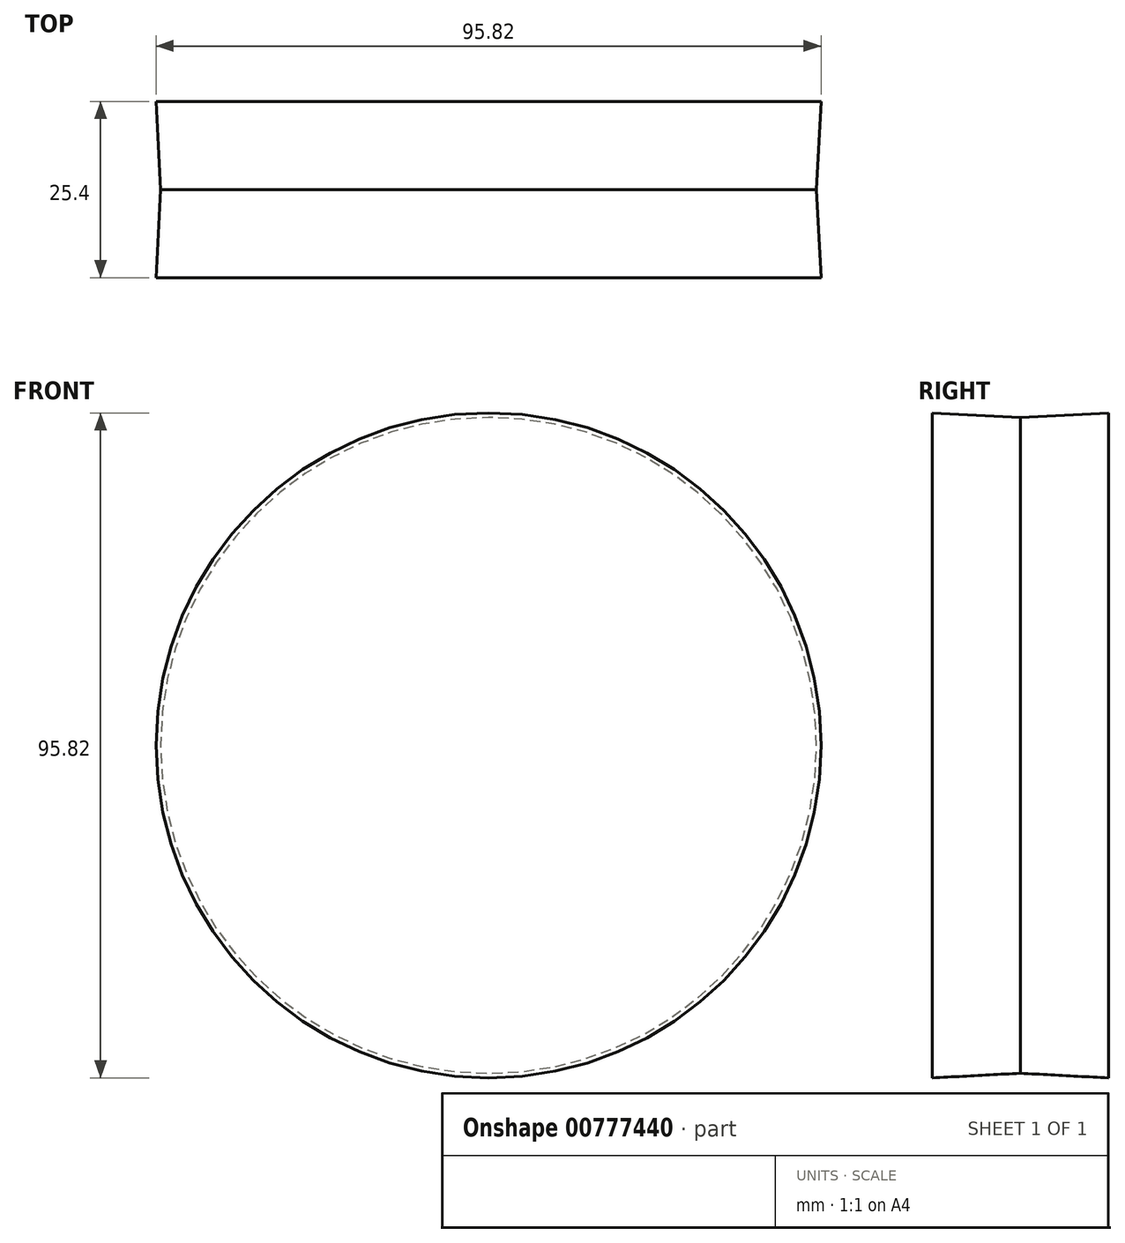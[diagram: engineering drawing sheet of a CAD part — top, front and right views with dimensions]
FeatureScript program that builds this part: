
annotation { "Feature Type Name" : "Feature", "Feature Type Description" : "" }
export const myFeature = defineFeature(function(context is Context, id is Id, definition is map)
    precondition{}
    {
        {
            var Q0;
            Q0=qCreatedBy(makeId("Front.planeOp"),FACE);
            var sketch = newSketch(context, id + "F0", { "sketchPlane" : qUnion([Q0])});
            skCircle(sketch, "E0", {"center": v(0, 0) * mm, "radius": 47.25 * mm});
            skSolve(sketch);
        }
        {
            var Q0;
            Q0=makeQuery(id+"F0.imprint","IMPRINT",FACE,{"disambiguationData":[TD([[makeQuery(id+"F0.imprint","IMPRINT",EDGE,{"derivedFrom":sQuery(id+"F0.wireOp",EDGE,"E0")}),1.0]])]});
            extrude(context, id + "F1", {"entities" : qUnion([Q0]), "endBound" : BoundingType.SYMMETRIC, "depth" : 25.4 * mm, "offsetDistance" : 25.4 * mm, "hasDraft" : true, "draftAngle" : 3 * degree});
        }
    });
